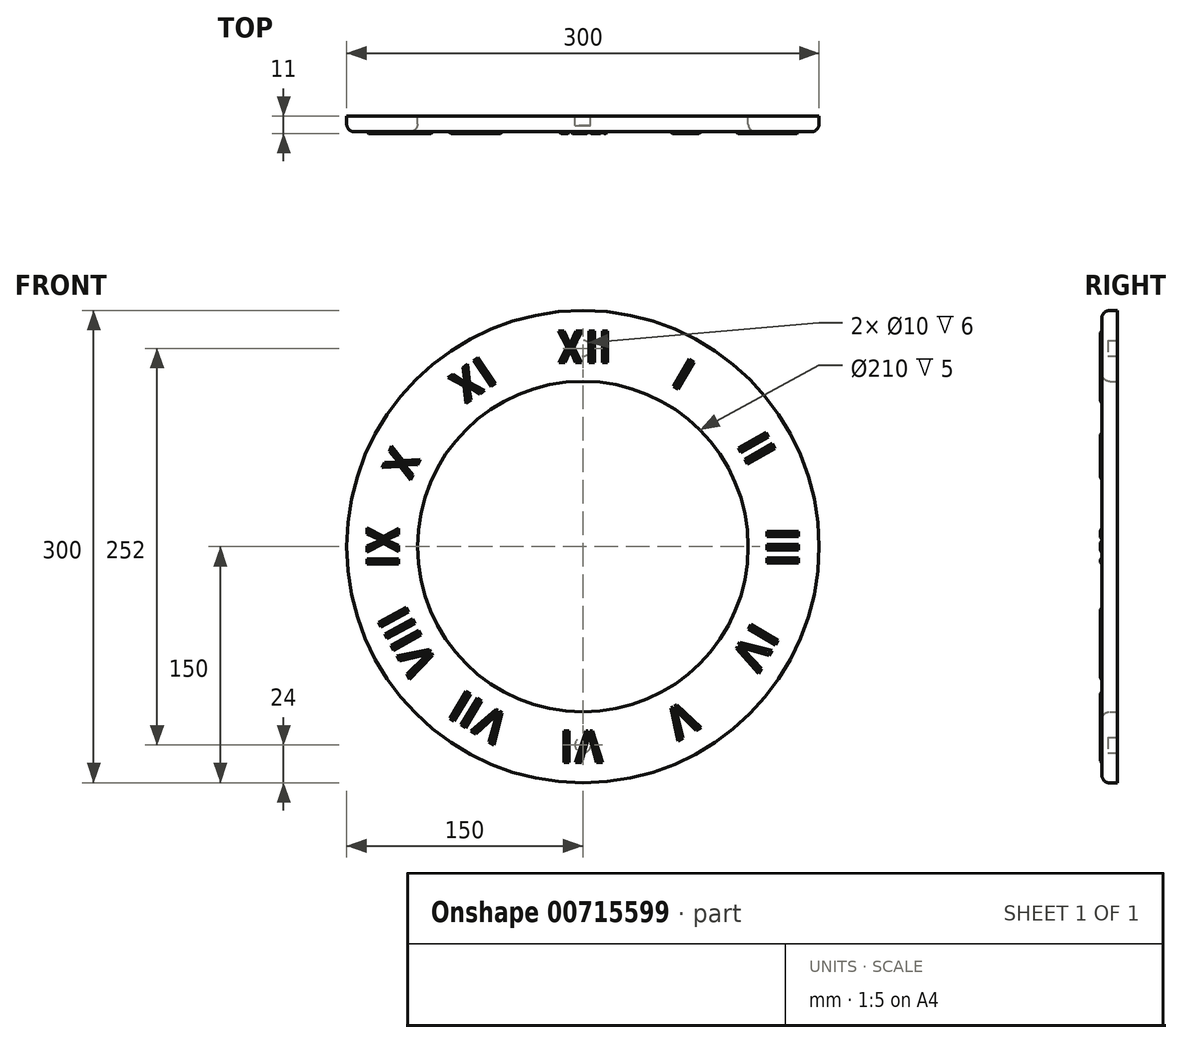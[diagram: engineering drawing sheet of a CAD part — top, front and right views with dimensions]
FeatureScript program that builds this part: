
annotation { "Feature Type Name" : "Feature", "Feature Type Description" : "" }
export const myFeature = defineFeature(function(context is Context, id is Id, definition is map)
    precondition{}
    {
        {
            var Q0;
            Q0=qCreatedBy(makeId("Front.planeOp"),FACE);
            var sketch = newSketch(context, id + "F0", { "sketchPlane" : qUnion([Q0])});
            skCircle(sketch, "E0", {"center": v(0, 0) * mm, "radius": 105 * mm});
            skCircle(sketch, "E1", {"center": v(0, 0) * mm, "radius": 150 * mm});
            skSolve(sketch);
        }
        {
            var Q0;
            Q0 = qSketchRegion(id + "F0", true);
            extrude(context, id + "F1", {"entities" : qUnion([Q0]), "depth" : 10 * mm, "offsetDistance" : 25 * mm});
        }
        {
            var Q0;
            Q0=makeQuery(id+"F1.opExtrude","CAP_FACE",FACE,{"disambiguationData":[OSD([sQuery(id+"F0.wireOp",EDGE,"E0"),sQuery(id+"F0.wireOp",EDGE,"E1")])],"isStart":true});
            var sketch = newSketch(context, id + "F2", { "sketchPlane" : qUnion([Q0])});
            skCircle(sketch, "E2", {"center": v(0, 126) * mm, "radius": 5 * mm});
            skCircle(sketch, "E3", {"center": v(0, -126) * mm, "radius": 5 * mm});
            skSolve(sketch);
        }
        {
            var Q0;
            Q0 = qSketchRegion(id + "F2", true);
            extrude(context, id + "F3", {"entities" : qUnion([Q0]), "operationType" : NewBodyOperationType.REMOVE, "oppositeDirection" : true, "depth" : 6 * mm, "offsetDistance" : 25 * mm});
        }
        {
            var Q0;
            Q0=makeQuery(id+"F1.opExtrude","CAP_EDGE",EDGE,{"disambiguationData":[OSD([sQuery(id+"F0.wireOp",EDGE,"E1")])],"isStart":false});
            var Q1;
            Q1=makeQuery(id+"F1.opExtrude","CAP_EDGE",EDGE,{"disambiguationData":[OSD([sQuery(id+"F0.wireOp",EDGE,"E0")])],"isStart":false});
            fillet(context, id + "F4", {"entities" : qUnion([Q0, Q1]), "radius" : 5 * mm, "tangentPropagation" : true, "allowEdgeOverflow" : false});
        }
        {
            var Q0;
            Q0=qCreatedBy(makeId("Front.planeOp"),FACE);
            cPlane(context, id + "F5", {"entities" : qUnion([Q0]), "cplaneType" : CPlaneType.OFFSET, "offset" : 10 * mm, "width" : 150 * mm, "height" : 150 * mm});
        }
        {
            var Q0;
            Q0=qCreatedBy(id+"F5.planeOp",FACE);
            var sketch = newSketch(context, id + "F6", { "sketchPlane" : qUnion([Q0])});
            skCircle(sketch, "E4.0.0", {"center": v(0, 0) * mm, "radius": 145 * mm});
            skText(sketch, "E5", { "text": "XII ", "fontName": "AllertaStencil-Regular.ttf"});
            skText(sketch, "E6", { "text": "I", "fontName": "AllertaStencil-Regular.ttf"});
            skText(sketch, "E7", { "text": "II", "fontName": "AllertaStencil-Regular.ttf"});
            skText(sketch, "E8", { "text": "III", "fontName": "AllertaStencil-Regular.ttf"});
            skText(sketch, "E9", { "text": "IV", "fontName": "AllertaStencil-Regular.ttf"});
            skText(sketch, "E10", { "text": "V", "fontName": "AllertaStencil-Regular.ttf"});
            skText(sketch, "E11", { "text": "VI", "fontName": "AllertaStencil-Regular.ttf"});
            skText(sketch, "E12", { "text": "VII", "fontName": "AllertaStencil-Regular.ttf"});
            skText(sketch, "E13", { "text": "VIII", "fontName": "AllertaStencil-Regular.ttf"});
            skText(sketch, "E14", { "text": "IX", "fontName": "AllertaStencil-Regular.ttf"});
            skText(sketch, "E15", { "text": "X", "fontName": "AllertaStencil-Regular.ttf"});
            skText(sketch, "E16", { "text": "XI", "fontName": "AllertaStencil-Regular.ttf"});
            skCircle(sketch, "E17.1.0", {"center": v(-0.56, -0.98) * mm, "radius": 145 * mm});
            skCircle(sketch, "E17.2.0", {"center": v(0.56, -0.98) * mm, "radius": 145 * mm});
            const initialGuessF6  = {"E5": [-0.01756, 0.117, 1, 0, 0.02], "E6": [0.05548, 0.10308, 0.86448, -0.50266, 0.02], "E7": [0.09765, 0.06495, 0.49548, -0.86862, 0.02], "E8": [0.117, 0.01221, 0, -1, 0.02], "E9": [0.10808, -0.04706, -0.50816, -0.86126, 0.02], "E10": [0.06664, -0.0967, -0.86966, -0.49365, 0.02], "E11": [0.01394, -0.117, -1, 0, 0.02], "E12": [-0.04477, -0.1096, -0.85698, 0.51534, 0.02], "E13": [-0.09171, -0.076, -0.48264, 0.87582, 0.02], "E14": [-0.117, -0.01364, 0, 1, 0.02], "E15": [-0.11032, 0.0401, 0.41627, 0.90924, 0.02], "E16": [-0.07622, 0.08977, 0.83087, 0.55647, 0.02]};
            skSetInitialGuess(sketch, initialGuessF6);
            skSolve(sketch);
        }
        {
            var Q0;
            Q0=makeQuery(id+"F6.imprint","IMPRINT",FACE,{"disambiguationData":[TD([[makeQuery(id+"F6.imprint","IMPRINT",EDGE,{"derivedFrom":sQuery(id+"F6.wireOp",EDGE,"E12.sketch_text.stroke-0")}),-1.0]])]});
            var Q1;
            Q1=makeQuery(id+"F6.imprint","IMPRINT",FACE,{"disambiguationData":[TD([[makeQuery(id+"F6.imprint","IMPRINT",EDGE,{"derivedFrom":sQuery(id+"F6.wireOp",EDGE,"E12.sketch_text.stroke-9")}),-1.0]])]});
            var Q2;
            Q2=makeQuery(id+"F6.imprint","IMPRINT",FACE,{"disambiguationData":[TD([[makeQuery(id+"F6.imprint","IMPRINT",EDGE,{"derivedFrom":sQuery(id+"F6.wireOp",EDGE,"E12.sketch_text.stroke-13")}),-1.0]])]});
            var Q3;
            Q3=makeQuery(id+"F6.imprint","IMPRINT",FACE,{"disambiguationData":[TD([[makeQuery(id+"F6.imprint","IMPRINT",EDGE,{"derivedFrom":sQuery(id+"F6.wireOp",EDGE,"E13.sketch_text.stroke-0")}),-1.0]])]});
            var Q4;
            Q4=makeQuery(id+"F6.imprint","IMPRINT",FACE,{"disambiguationData":[TD([[makeQuery(id+"F6.imprint","IMPRINT",EDGE,{"derivedFrom":sQuery(id+"F6.wireOp",EDGE,"E13.sketch_text.stroke-9")}),-1.0]])]});
            var Q5;
            Q5=makeQuery(id+"F6.imprint","IMPRINT",FACE,{"disambiguationData":[TD([[makeQuery(id+"F6.imprint","IMPRINT",EDGE,{"derivedFrom":sQuery(id+"F6.wireOp",EDGE,"E13.sketch_text.stroke-13")}),-1.0]])]});
            var Q6;
            Q6=makeQuery(id+"F6.imprint","IMPRINT",FACE,{"disambiguationData":[TD([[makeQuery(id+"F6.imprint","IMPRINT",EDGE,{"derivedFrom":sQuery(id+"F6.wireOp",EDGE,"E13.sketch_text.stroke-17")}),-1.0]])]});
            var Q7;
            Q7=makeQuery(id+"F6.imprint","IMPRINT",FACE,{"disambiguationData":[TD([[makeQuery(id+"F6.imprint","IMPRINT",EDGE,{"derivedFrom":sQuery(id+"F6.wireOp",EDGE,"E14.sketch_text.stroke-0")}),-1.0]])]});
            var Q8;
            Q8=makeQuery(id+"F6.imprint","IMPRINT",FACE,{"disambiguationData":[TD([[makeQuery(id+"F6.imprint","IMPRINT",EDGE,{"derivedFrom":sQuery(id+"F6.wireOp",EDGE,"E14.sketch_text.stroke-4")}),-1.0]])]});
            var Q9;
            Q9=makeQuery(id+"F6.imprint","IMPRINT",FACE,{"disambiguationData":[TD([[makeQuery(id+"F6.imprint","IMPRINT",EDGE,{"derivedFrom":sQuery(id+"F6.wireOp",EDGE,"E15.sketch_text.stroke-0")}),-1.0]])]});
            var Q10;
            Q10=makeQuery(id+"F6.imprint","IMPRINT",FACE,{"disambiguationData":[TD([[makeQuery(id+"F6.imprint","IMPRINT",EDGE,{"derivedFrom":sQuery(id+"F6.wireOp",EDGE,"E16.sketch_text.stroke-0")}),-1.0]])]});
            var Q11;
            Q11=makeQuery(id+"F6.imprint","IMPRINT",FACE,{"disambiguationData":[TD([[makeQuery(id+"F6.imprint","IMPRINT",EDGE,{"derivedFrom":sQuery(id+"F6.wireOp",EDGE,"E16.sketch_text.stroke-12")}),-1.0]])]});
            var Q12;
            Q12=makeQuery(id+"F6.imprint","IMPRINT",FACE,{"disambiguationData":[TD([[makeQuery(id+"F6.imprint","IMPRINT",EDGE,{"derivedFrom":sQuery(id+"F6.wireOp",EDGE,"E5.sketch_text.stroke-0")}),-1.0]])]});
            var Q13;
            Q13=makeQuery(id+"F6.imprint","IMPRINT",FACE,{"disambiguationData":[TD([[makeQuery(id+"F6.imprint","IMPRINT",EDGE,{"derivedFrom":sQuery(id+"F6.wireOp",EDGE,"E5.sketch_text.stroke-12")}),-1.0]])]});
            var Q14;
            Q14=makeQuery(id+"F6.imprint","IMPRINT",FACE,{"disambiguationData":[TD([[makeQuery(id+"F6.imprint","IMPRINT",EDGE,{"derivedFrom":sQuery(id+"F6.wireOp",EDGE,"E5.sketch_text.stroke-16")}),-1.0]])]});
            var Q15;
            Q15=makeQuery(id+"F6.imprint","IMPRINT",FACE,{"disambiguationData":[TD([[makeQuery(id+"F6.imprint","IMPRINT",EDGE,{"derivedFrom":sQuery(id+"F6.wireOp",EDGE,"E6.sketch_text.stroke-0")}),-1.0]])]});
            var Q16;
            Q16=makeQuery(id+"F6.imprint","IMPRINT",FACE,{"disambiguationData":[TD([[makeQuery(id+"F6.imprint","IMPRINT",EDGE,{"derivedFrom":sQuery(id+"F6.wireOp",EDGE,"E7.sketch_text.stroke-0")}),-1.0]])]});
            var Q17;
            Q17=makeQuery(id+"F6.imprint","IMPRINT",FACE,{"disambiguationData":[TD([[makeQuery(id+"F6.imprint","IMPRINT",EDGE,{"derivedFrom":sQuery(id+"F6.wireOp",EDGE,"E7.sketch_text.stroke-4")}),-1.0]])]});
            var Q18;
            Q18=makeQuery(id+"F6.imprint","IMPRINT",FACE,{"disambiguationData":[TD([[makeQuery(id+"F6.imprint","IMPRINT",EDGE,{"derivedFrom":sQuery(id+"F6.wireOp",EDGE,"E8.sketch_text.stroke-0")}),-1.0]])]});
            var Q19;
            Q19=makeQuery(id+"F6.imprint","IMPRINT",FACE,{"disambiguationData":[TD([[makeQuery(id+"F6.imprint","IMPRINT",EDGE,{"derivedFrom":sQuery(id+"F6.wireOp",EDGE,"E8.sketch_text.stroke-4")}),-1.0]])]});
            var Q20;
            Q20=makeQuery(id+"F6.imprint","IMPRINT",FACE,{"disambiguationData":[TD([[makeQuery(id+"F6.imprint","IMPRINT",EDGE,{"derivedFrom":sQuery(id+"F6.wireOp",EDGE,"E8.sketch_text.stroke-8")}),-1.0]])]});
            var Q21;
            Q21=makeQuery(id+"F6.imprint","IMPRINT",FACE,{"disambiguationData":[TD([[makeQuery(id+"F6.imprint","IMPRINT",EDGE,{"derivedFrom":sQuery(id+"F6.wireOp",EDGE,"E9.sketch_text.stroke-0")}),-1.0]])]});
            var Q22;
            Q22=makeQuery(id+"F6.imprint","IMPRINT",FACE,{"disambiguationData":[TD([[makeQuery(id+"F6.imprint","IMPRINT",EDGE,{"derivedFrom":sQuery(id+"F6.wireOp",EDGE,"E9.sketch_text.stroke-4")}),-1.0]])]});
            var Q23;
            Q23=makeQuery(id+"F6.imprint","IMPRINT",FACE,{"disambiguationData":[TD([[makeQuery(id+"F6.imprint","IMPRINT",EDGE,{"derivedFrom":sQuery(id+"F6.wireOp",EDGE,"E10.sketch_text.stroke-0")}),-1.0]])]});
            var Q24;
            Q24=makeQuery(id+"F6.imprint","IMPRINT",FACE,{"disambiguationData":[TD([[makeQuery(id+"F6.imprint","IMPRINT",EDGE,{"derivedFrom":sQuery(id+"F6.wireOp",EDGE,"E11.sketch_text.stroke-0")}),-1.0]])]});
            var Q25;
            Q25=makeQuery(id+"F6.imprint","IMPRINT",FACE,{"disambiguationData":[TD([[makeQuery(id+"F6.imprint","IMPRINT",EDGE,{"derivedFrom":sQuery(id+"F6.wireOp",EDGE,"E11.sketch_text.stroke-9")}),-1.0]])]});
            var Q26;
            Q26=makeQuery(id+"F6.imprint","IMPRINT",FACE,{"disambiguationData":[TD([[makeQuery(id+"F6.imprint","IMPRINT",EDGE,{"derivedFrom":sQuery(id+"F6.wireOp",EDGE,"E5.sketch_text.stroke-18")}),-1.0]])]});
            var Q27;
            Q27=makeQuery(id+"F6.imprint","IMPRINT",FACE,{"disambiguationData":[TD([[makeQuery(id+"F6.imprint","IMPRINT",EDGE,{"derivedFrom":sQuery(id+"F6.wireOp",EDGE,"E15.sketch_text.stroke-7")}),-1.0]])]});
            var Q28;
            Q28=makeQuery(id+"F6.imprint","IMPRINT",FACE,{"disambiguationData":[TD([[makeQuery(id+"F6.imprint","IMPRINT",EDGE,{"derivedFrom":sQuery(id+"F6.wireOp",EDGE,"E14.sketch_text.stroke-11")}),-1.0]])]});
            var Q29;
            Q29=makeQuery(id+"F6.imprint","IMPRINT",FACE,{"disambiguationData":[TD([[makeQuery(id+"F6.imprint","IMPRINT",EDGE,{"derivedFrom":sQuery(id+"F6.wireOp",EDGE,"E12.sketch_text.stroke-14")}),-1.0]])]});
            var Q30;
            Q30=makeQuery(id+"F6.imprint","IMPRINT",FACE,{"disambiguationData":[TD([[makeQuery(id+"F6.imprint","IMPRINT",EDGE,{"derivedFrom":sQuery(id+"F6.wireOp",EDGE,"E11.sketch_text.stroke-10")}),-1.0]])]});
            var Q31;
            Q31=makeQuery(id+"F6.imprint","IMPRINT",FACE,{"disambiguationData":[TD([[makeQuery(id+"F6.imprint","IMPRINT",EDGE,{"derivedFrom":sQuery(id+"F6.wireOp",EDGE,"E10.sketch_text.stroke-5")}),-1.0]])]});
            var Q32;
            Q32=makeQuery(id+"F6.imprint","IMPRINT",FACE,{"disambiguationData":[TD([[makeQuery(id+"F6.imprint","IMPRINT",EDGE,{"derivedFrom":sQuery(id+"F6.wireOp",EDGE,"E9.sketch_text.stroke-9")}),-1.0]])]});
            var Q33;
            Q33=makeQuery(id+"F6.imprint","IMPRINT",FACE,{"disambiguationData":[TD([[makeQuery(id+"F6.imprint","IMPRINT",EDGE,{"derivedFrom":sQuery(id+"F6.wireOp",EDGE,"E16.sketch_text.stroke-14")}),-1.0]])]});
            var Q34;
            Q34=makeQuery(id+"F6.imprint","IMPRINT",FACE,{"disambiguationData":[TD([[makeQuery(id+"F6.imprint","IMPRINT",EDGE,{"derivedFrom":sQuery(id+"F6.wireOp",EDGE,"E13.sketch_text.stroke-18")}),-1.0]])]});
            extrude(context, id + "F7", {"entities" : qUnion([Q0, Q1, Q2, Q3, Q4, Q5, Q6, Q7, Q8, Q9, Q10, Q11, Q12, Q13, Q14, Q15, Q16, Q17, Q18, Q19, Q20, Q21, Q22, Q23, Q24, Q25, Q26, Q27, Q28, Q29, Q30, Q31, Q32, Q33, Q34]), "operationType" : NewBodyOperationType.ADD, "depth" : 1 * mm, "offsetDistance" : 25 * mm});
        }
        {
            var Q0;
            Q0=makeQuery(id+"F7.opExtrude","CAP_FACE",FACE,{"disambiguationData":[OSD([sQuery(id+"F6.wireOp",EDGE,"E5.sketch_text.stroke-18"),sQuery(id+"F6.wireOp",EDGE,"E5.sketch_text.stroke-19"),sQuery(id+"F6.wireOp",EDGE,"E5.sketch_text.stroke-20"),sQuery(id+"F6.wireOp",EDGE,"E5.sketch_text.stroke-21")])],"isStart":false});
            var Q1;
            Q1=makeQuery(id+"F7.opExtrude","CAP_FACE",FACE,{"disambiguationData":[OSD([sQuery(id+"F6.wireOp",EDGE,"E5.sketch_text.stroke-14"),sQuery(id+"F6.wireOp",EDGE,"E5.sketch_text.stroke-15"),sQuery(id+"F6.wireOp",EDGE,"E5.sketch_text.stroke-16"),sQuery(id+"F6.wireOp",EDGE,"E5.sketch_text.stroke-17")])],"isStart":false});
            var Q2;
            Q2=makeQuery(id+"F7.opExtrude","CAP_FACE",FACE,{"disambiguationData":[OSD([sQuery(id+"F6.wireOp",EDGE,"E5.sketch_text.stroke-7"),sQuery(id+"F6.wireOp",EDGE,"E5.sketch_text.stroke-8"),sQuery(id+"F6.wireOp",EDGE,"E5.sketch_text.stroke-9"),sQuery(id+"F6.wireOp",EDGE,"E5.sketch_text.stroke-10"),sQuery(id+"F6.wireOp",EDGE,"E5.sketch_text.stroke-11"),sQuery(id+"F6.wireOp",EDGE,"E5.sketch_text.stroke-12"),sQuery(id+"F6.wireOp",EDGE,"E5.sketch_text.stroke-13")])],"isStart":false});
            var Q3;
            Q3=makeQuery(id+"F7.opExtrude","CAP_FACE",FACE,{"disambiguationData":[OSD([sQuery(id+"F6.wireOp",EDGE,"E5.sketch_text.stroke-0"),sQuery(id+"F6.wireOp",EDGE,"E5.sketch_text.stroke-1"),sQuery(id+"F6.wireOp",EDGE,"E5.sketch_text.stroke-2"),sQuery(id+"F6.wireOp",EDGE,"E5.sketch_text.stroke-3"),sQuery(id+"F6.wireOp",EDGE,"E5.sketch_text.stroke-4"),sQuery(id+"F6.wireOp",EDGE,"E5.sketch_text.stroke-5"),sQuery(id+"F6.wireOp",EDGE,"E5.sketch_text.stroke-6")])],"isStart":false});
            var Q4;
            Q4=makeQuery(id+"F7.opExtrude","CAP_FACE",FACE,{"disambiguationData":[OSD([sQuery(id+"F6.wireOp",EDGE,"E16.sketch_text.stroke-14"),sQuery(id+"F6.wireOp",EDGE,"E16.sketch_text.stroke-15"),sQuery(id+"F6.wireOp",EDGE,"E16.sketch_text.stroke-16"),sQuery(id+"F6.wireOp",EDGE,"E16.sketch_text.stroke-17")])],"isStart":false});
            var Q5;
            Q5=makeQuery(id+"F7.opExtrude","CAP_FACE",FACE,{"disambiguationData":[OSD([sQuery(id+"F6.wireOp",EDGE,"E16.sketch_text.stroke-7"),sQuery(id+"F6.wireOp",EDGE,"E16.sketch_text.stroke-8"),sQuery(id+"F6.wireOp",EDGE,"E16.sketch_text.stroke-9"),sQuery(id+"F6.wireOp",EDGE,"E16.sketch_text.stroke-10"),sQuery(id+"F6.wireOp",EDGE,"E16.sketch_text.stroke-11"),sQuery(id+"F6.wireOp",EDGE,"E16.sketch_text.stroke-12"),sQuery(id+"F6.wireOp",EDGE,"E16.sketch_text.stroke-13")])],"isStart":false});
            var Q6;
            Q6=makeQuery(id+"F7.opExtrude","CAP_FACE",FACE,{"disambiguationData":[OSD([sQuery(id+"F6.wireOp",EDGE,"E16.sketch_text.stroke-0"),sQuery(id+"F6.wireOp",EDGE,"E16.sketch_text.stroke-1"),sQuery(id+"F6.wireOp",EDGE,"E16.sketch_text.stroke-2"),sQuery(id+"F6.wireOp",EDGE,"E16.sketch_text.stroke-3"),sQuery(id+"F6.wireOp",EDGE,"E16.sketch_text.stroke-4"),sQuery(id+"F6.wireOp",EDGE,"E16.sketch_text.stroke-5"),sQuery(id+"F6.wireOp",EDGE,"E16.sketch_text.stroke-6")])],"isStart":false});
            var Q7;
            Q7=makeQuery(id+"F7.opExtrude","CAP_FACE",FACE,{"disambiguationData":[OSD([sQuery(id+"F6.wireOp",EDGE,"E15.sketch_text.stroke-7"),sQuery(id+"F6.wireOp",EDGE,"E15.sketch_text.stroke-8"),sQuery(id+"F6.wireOp",EDGE,"E15.sketch_text.stroke-9"),sQuery(id+"F6.wireOp",EDGE,"E15.sketch_text.stroke-10"),sQuery(id+"F6.wireOp",EDGE,"E15.sketch_text.stroke-11"),sQuery(id+"F6.wireOp",EDGE,"E15.sketch_text.stroke-12"),sQuery(id+"F6.wireOp",EDGE,"E15.sketch_text.stroke-13")])],"isStart":false});
            var Q8;
            Q8=makeQuery(id+"F7.opExtrude","CAP_FACE",FACE,{"disambiguationData":[OSD([sQuery(id+"F6.wireOp",EDGE,"E15.sketch_text.stroke-0"),sQuery(id+"F6.wireOp",EDGE,"E15.sketch_text.stroke-1"),sQuery(id+"F6.wireOp",EDGE,"E15.sketch_text.stroke-2"),sQuery(id+"F6.wireOp",EDGE,"E15.sketch_text.stroke-3"),sQuery(id+"F6.wireOp",EDGE,"E15.sketch_text.stroke-4"),sQuery(id+"F6.wireOp",EDGE,"E15.sketch_text.stroke-5"),sQuery(id+"F6.wireOp",EDGE,"E15.sketch_text.stroke-6")])],"isStart":false});
            var Q9;
            Q9=makeQuery(id+"F7.opExtrude","CAP_FACE",FACE,{"disambiguationData":[OSD([sQuery(id+"F6.wireOp",EDGE,"E14.sketch_text.stroke-11"),sQuery(id+"F6.wireOp",EDGE,"E14.sketch_text.stroke-12"),sQuery(id+"F6.wireOp",EDGE,"E14.sketch_text.stroke-13"),sQuery(id+"F6.wireOp",EDGE,"E14.sketch_text.stroke-14"),sQuery(id+"F6.wireOp",EDGE,"E14.sketch_text.stroke-15"),sQuery(id+"F6.wireOp",EDGE,"E14.sketch_text.stroke-16"),sQuery(id+"F6.wireOp",EDGE,"E14.sketch_text.stroke-17")])],"isStart":false});
            var Q10;
            Q10=makeQuery(id+"F7.opExtrude","CAP_FACE",FACE,{"disambiguationData":[OSD([sQuery(id+"F6.wireOp",EDGE,"E14.sketch_text.stroke-4"),sQuery(id+"F6.wireOp",EDGE,"E14.sketch_text.stroke-5"),sQuery(id+"F6.wireOp",EDGE,"E14.sketch_text.stroke-6"),sQuery(id+"F6.wireOp",EDGE,"E14.sketch_text.stroke-7"),sQuery(id+"F6.wireOp",EDGE,"E14.sketch_text.stroke-8"),sQuery(id+"F6.wireOp",EDGE,"E14.sketch_text.stroke-9"),sQuery(id+"F6.wireOp",EDGE,"E14.sketch_text.stroke-10")])],"isStart":false});
            var Q11;
            Q11=makeQuery(id+"F7.opExtrude","CAP_FACE",FACE,{"disambiguationData":[OSD([sQuery(id+"F6.wireOp",EDGE,"E14.sketch_text.stroke-0"),sQuery(id+"F6.wireOp",EDGE,"E14.sketch_text.stroke-1"),sQuery(id+"F6.wireOp",EDGE,"E14.sketch_text.stroke-2"),sQuery(id+"F6.wireOp",EDGE,"E14.sketch_text.stroke-3")])],"isStart":false});
            var Q12;
            Q12=makeQuery(id+"F7.opExtrude","CAP_FACE",FACE,{"disambiguationData":[OSD([sQuery(id+"F6.wireOp",EDGE,"E13.sketch_text.stroke-18"),sQuery(id+"F6.wireOp",EDGE,"E13.sketch_text.stroke-19"),sQuery(id+"F6.wireOp",EDGE,"E13.sketch_text.stroke-20"),sQuery(id+"F6.wireOp",EDGE,"E13.sketch_text.stroke-21")])],"isStart":false});
            var Q13;
            Q13=makeQuery(id+"F7.opExtrude","CAP_FACE",FACE,{"disambiguationData":[OSD([sQuery(id+"F6.wireOp",EDGE,"E13.sketch_text.stroke-14"),sQuery(id+"F6.wireOp",EDGE,"E13.sketch_text.stroke-15"),sQuery(id+"F6.wireOp",EDGE,"E13.sketch_text.stroke-16"),sQuery(id+"F6.wireOp",EDGE,"E13.sketch_text.stroke-17")])],"isStart":false});
            var Q14;
            Q14=makeQuery(id+"F7.opExtrude","CAP_FACE",FACE,{"disambiguationData":[OSD([sQuery(id+"F6.wireOp",EDGE,"E13.sketch_text.stroke-10"),sQuery(id+"F6.wireOp",EDGE,"E13.sketch_text.stroke-11"),sQuery(id+"F6.wireOp",EDGE,"E13.sketch_text.stroke-12"),sQuery(id+"F6.wireOp",EDGE,"E13.sketch_text.stroke-13")])],"isStart":false});
            var Q15;
            Q15=makeQuery(id+"F7.opExtrude","CAP_FACE",FACE,{"disambiguationData":[OSD([sQuery(id+"F6.wireOp",EDGE,"E12.sketch_text.stroke-14"),sQuery(id+"F6.wireOp",EDGE,"E12.sketch_text.stroke-15"),sQuery(id+"F6.wireOp",EDGE,"E12.sketch_text.stroke-16"),sQuery(id+"F6.wireOp",EDGE,"E12.sketch_text.stroke-17")])],"isStart":false});
            var Q16;
            Q16=makeQuery(id+"F7.opExtrude","CAP_FACE",FACE,{"disambiguationData":[OSD([sQuery(id+"F6.wireOp",EDGE,"E12.sketch_text.stroke-10"),sQuery(id+"F6.wireOp",EDGE,"E12.sketch_text.stroke-11"),sQuery(id+"F6.wireOp",EDGE,"E12.sketch_text.stroke-12"),sQuery(id+"F6.wireOp",EDGE,"E12.sketch_text.stroke-13")])],"isStart":false});
            var Q17;
            Q17=makeQuery(id+"F7.opExtrude","CAP_FACE",FACE,{"disambiguationData":[OSD([sQuery(id+"F6.wireOp",EDGE,"E11.sketch_text.stroke-10"),sQuery(id+"F6.wireOp",EDGE,"E11.sketch_text.stroke-11"),sQuery(id+"F6.wireOp",EDGE,"E11.sketch_text.stroke-12"),sQuery(id+"F6.wireOp",EDGE,"E11.sketch_text.stroke-13")])],"isStart":false});
            var Q18;
            Q18=makeQuery(id+"F7.opExtrude","CAP_FACE",FACE,{"disambiguationData":[OSD([sQuery(id+"F6.wireOp",EDGE,"E9.sketch_text.stroke-0"),sQuery(id+"F6.wireOp",EDGE,"E9.sketch_text.stroke-1"),sQuery(id+"F6.wireOp",EDGE,"E9.sketch_text.stroke-2"),sQuery(id+"F6.wireOp",EDGE,"E9.sketch_text.stroke-3")])],"isStart":false});
            var Q19;
            Q19=makeQuery(id+"F7.opExtrude","CAP_FACE",FACE,{"disambiguationData":[OSD([sQuery(id+"F6.wireOp",EDGE,"E8.sketch_text.stroke-4"),sQuery(id+"F6.wireOp",EDGE,"E8.sketch_text.stroke-5"),sQuery(id+"F6.wireOp",EDGE,"E8.sketch_text.stroke-6"),sQuery(id+"F6.wireOp",EDGE,"E8.sketch_text.stroke-7")])],"isStart":false});
            var Q20;
            Q20=makeQuery(id+"F7.opExtrude","CAP_FACE",FACE,{"disambiguationData":[OSD([sQuery(id+"F6.wireOp",EDGE,"E8.sketch_text.stroke-0"),sQuery(id+"F6.wireOp",EDGE,"E8.sketch_text.stroke-1"),sQuery(id+"F6.wireOp",EDGE,"E8.sketch_text.stroke-2"),sQuery(id+"F6.wireOp",EDGE,"E8.sketch_text.stroke-3")])],"isStart":false});
            var Q21;
            Q21=makeQuery(id+"F7.opExtrude","CAP_FACE",FACE,{"disambiguationData":[OSD([sQuery(id+"F6.wireOp",EDGE,"E8.sketch_text.stroke-8"),sQuery(id+"F6.wireOp",EDGE,"E8.sketch_text.stroke-9"),sQuery(id+"F6.wireOp",EDGE,"E8.sketch_text.stroke-10"),sQuery(id+"F6.wireOp",EDGE,"E8.sketch_text.stroke-11")])],"isStart":false});
            var Q22;
            Q22=makeQuery(id+"F7.opExtrude","CAP_FACE",FACE,{"disambiguationData":[OSD([sQuery(id+"F6.wireOp",EDGE,"E7.sketch_text.stroke-4"),sQuery(id+"F6.wireOp",EDGE,"E7.sketch_text.stroke-5"),sQuery(id+"F6.wireOp",EDGE,"E7.sketch_text.stroke-6"),sQuery(id+"F6.wireOp",EDGE,"E7.sketch_text.stroke-7")])],"isStart":false});
            var Q23;
            Q23=makeQuery(id+"F7.opExtrude","CAP_FACE",FACE,{"disambiguationData":[OSD([sQuery(id+"F6.wireOp",EDGE,"E7.sketch_text.stroke-0"),sQuery(id+"F6.wireOp",EDGE,"E7.sketch_text.stroke-1"),sQuery(id+"F6.wireOp",EDGE,"E7.sketch_text.stroke-2"),sQuery(id+"F6.wireOp",EDGE,"E7.sketch_text.stroke-3")])],"isStart":false});
            var Q24;
            Q24=makeQuery(id+"F7.opExtrude","CAP_FACE",FACE,{"disambiguationData":[OSD([sQuery(id+"F6.wireOp",EDGE,"E6.sketch_text.stroke-0"),sQuery(id+"F6.wireOp",EDGE,"E6.sketch_text.stroke-1"),sQuery(id+"F6.wireOp",EDGE,"E6.sketch_text.stroke-2"),sQuery(id+"F6.wireOp",EDGE,"E6.sketch_text.stroke-3")])],"isStart":false});
            chamfer(context, id + "F8", {"entities" : qUnion([Q0, Q1, Q2, Q3, Q4, Q5, Q6, Q7, Q8, Q9, Q10, Q11, Q12, Q13, Q14, Q15, Q16, Q17, Q18, Q19, Q20, Q21, Q22, Q23, Q24]), "width" : 1 * mm, "tangentPropagation" : true});
        }
        {
            var Q0;
            Q0=makeQuery(id+"F7.opExtrude","CAP_FACE",FACE,{"disambiguationData":[OSD([sQuery(id+"F6.wireOp",EDGE,"E13.sketch_text.stroke-5"),sQuery(id+"F6.wireOp",EDGE,"E13.sketch_text.stroke-6"),sQuery(id+"F6.wireOp",EDGE,"E13.sketch_text.stroke-7"),sQuery(id+"F6.wireOp",EDGE,"E13.sketch_text.stroke-8"),sQuery(id+"F6.wireOp",EDGE,"E13.sketch_text.stroke-9")])],"isStart":false});
            var Q1;
            Q1=makeQuery(id+"F7.opExtrude","CAP_FACE",FACE,{"disambiguationData":[OSD([sQuery(id+"F6.wireOp",EDGE,"E13.sketch_text.stroke-0"),sQuery(id+"F6.wireOp",EDGE,"E13.sketch_text.stroke-1"),sQuery(id+"F6.wireOp",EDGE,"E13.sketch_text.stroke-2"),sQuery(id+"F6.wireOp",EDGE,"E13.sketch_text.stroke-3"),sQuery(id+"F6.wireOp",EDGE,"E13.sketch_text.stroke-4")])],"isStart":false});
            var Q2;
            Q2=makeQuery(id+"F7.opExtrude","CAP_FACE",FACE,{"disambiguationData":[OSD([sQuery(id+"F6.wireOp",EDGE,"E12.sketch_text.stroke-5"),sQuery(id+"F6.wireOp",EDGE,"E12.sketch_text.stroke-6"),sQuery(id+"F6.wireOp",EDGE,"E12.sketch_text.stroke-7"),sQuery(id+"F6.wireOp",EDGE,"E12.sketch_text.stroke-8"),sQuery(id+"F6.wireOp",EDGE,"E12.sketch_text.stroke-9")])],"isStart":false});
            var Q3;
            Q3=makeQuery(id+"F7.opExtrude","CAP_FACE",FACE,{"disambiguationData":[OSD([sQuery(id+"F6.wireOp",EDGE,"E12.sketch_text.stroke-0"),sQuery(id+"F6.wireOp",EDGE,"E12.sketch_text.stroke-1"),sQuery(id+"F6.wireOp",EDGE,"E12.sketch_text.stroke-2"),sQuery(id+"F6.wireOp",EDGE,"E12.sketch_text.stroke-3"),sQuery(id+"F6.wireOp",EDGE,"E12.sketch_text.stroke-4")])],"isStart":false});
            var Q4;
            Q4=makeQuery(id+"F7.opExtrude","CAP_FACE",FACE,{"disambiguationData":[OSD([sQuery(id+"F6.wireOp",EDGE,"E11.sketch_text.stroke-5"),sQuery(id+"F6.wireOp",EDGE,"E11.sketch_text.stroke-6"),sQuery(id+"F6.wireOp",EDGE,"E11.sketch_text.stroke-7"),sQuery(id+"F6.wireOp",EDGE,"E11.sketch_text.stroke-8"),sQuery(id+"F6.wireOp",EDGE,"E11.sketch_text.stroke-9")])],"isStart":false});
            var Q5;
            Q5=makeQuery(id+"F7.opExtrude","CAP_FACE",FACE,{"disambiguationData":[OSD([sQuery(id+"F6.wireOp",EDGE,"E11.sketch_text.stroke-0"),sQuery(id+"F6.wireOp",EDGE,"E11.sketch_text.stroke-1"),sQuery(id+"F6.wireOp",EDGE,"E11.sketch_text.stroke-2"),sQuery(id+"F6.wireOp",EDGE,"E11.sketch_text.stroke-3"),sQuery(id+"F6.wireOp",EDGE,"E11.sketch_text.stroke-4")])],"isStart":false});
            var Q6;
            Q6=makeQuery(id+"F7.opExtrude","CAP_FACE",FACE,{"disambiguationData":[OSD([sQuery(id+"F6.wireOp",EDGE,"E10.sketch_text.stroke-5"),sQuery(id+"F6.wireOp",EDGE,"E10.sketch_text.stroke-6"),sQuery(id+"F6.wireOp",EDGE,"E10.sketch_text.stroke-7"),sQuery(id+"F6.wireOp",EDGE,"E10.sketch_text.stroke-8"),sQuery(id+"F6.wireOp",EDGE,"E10.sketch_text.stroke-9")])],"isStart":false});
            var Q7;
            Q7=makeQuery(id+"F7.opExtrude","CAP_FACE",FACE,{"disambiguationData":[OSD([sQuery(id+"F6.wireOp",EDGE,"E10.sketch_text.stroke-0"),sQuery(id+"F6.wireOp",EDGE,"E10.sketch_text.stroke-1"),sQuery(id+"F6.wireOp",EDGE,"E10.sketch_text.stroke-2"),sQuery(id+"F6.wireOp",EDGE,"E10.sketch_text.stroke-3"),sQuery(id+"F6.wireOp",EDGE,"E10.sketch_text.stroke-4")])],"isStart":false});
            var Q8;
            Q8=makeQuery(id+"F7.opExtrude","CAP_FACE",FACE,{"disambiguationData":[OSD([sQuery(id+"F6.wireOp",EDGE,"E9.sketch_text.stroke-9"),sQuery(id+"F6.wireOp",EDGE,"E9.sketch_text.stroke-10"),sQuery(id+"F6.wireOp",EDGE,"E9.sketch_text.stroke-11"),sQuery(id+"F6.wireOp",EDGE,"E9.sketch_text.stroke-12"),sQuery(id+"F6.wireOp",EDGE,"E9.sketch_text.stroke-13")])],"isStart":false});
            var Q9;
            Q9=makeQuery(id+"F7.opExtrude","CAP_FACE",FACE,{"disambiguationData":[OSD([sQuery(id+"F6.wireOp",EDGE,"E9.sketch_text.stroke-4"),sQuery(id+"F6.wireOp",EDGE,"E9.sketch_text.stroke-5"),sQuery(id+"F6.wireOp",EDGE,"E9.sketch_text.stroke-6"),sQuery(id+"F6.wireOp",EDGE,"E9.sketch_text.stroke-7"),sQuery(id+"F6.wireOp",EDGE,"E9.sketch_text.stroke-8")])],"isStart":false});
            chamfer(context, id + "F9", {"entities" : qUnion([Q0, Q1, Q2, Q3, Q4, Q5, Q6, Q7, Q8, Q9]), "width" : .8 * mm, "tangentPropagation" : true});
        }
    });
